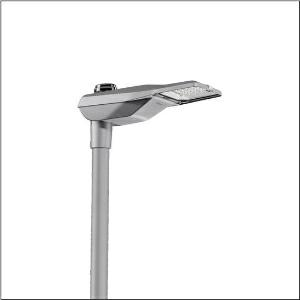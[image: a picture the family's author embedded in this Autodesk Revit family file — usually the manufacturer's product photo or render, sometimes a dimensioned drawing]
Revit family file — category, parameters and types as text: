
# Revit family: streetlight_sl_21_micro___stw1_0a_5xe5e37n08db_8c5c
name_source: partatom
category: Lighting Fixtures
units: mm (PartAtom-declared; Revit-internal decimal feet)

## family parameters
Cut with Voids When Loaded = No
Host = Face
Light Source = No
Part Type = Normal
Room Calculation Point = No
Round Connector Dimension = Use Diameter
Shared = No

## types (1)
- --- (1 x LED, 5110 lm, 39.1 W, 3000K)
    Apparent Load = 39 VA
    CIE Flux Codes = 38 75 98 100 100
    Color Rendering = 70
    Color Temperature = 3000K
    Default Elevation = 1800 mm
    Description = Streetlight SL 21 micro, mast luminaire, primary light control with lens, of PMMA, primary optical cover: cover, of toughened safety glass, transparent, light distribution: STW1.0a, light emission: direct distribution, primary light characteristic: asymmetric, installation type: post-top, LED, 3G 1.5mm², High Power LED, rated luminous flux: 5.110lm, luminous efficacy: 131lm/W, light colour: 730, colour temperature: 3000K, control: overheat protection, presetting dimming linear, constant luminous flux control, time-dependent luminous flux control, flexible luminous flux parameterisation, mains connection: 230..240V, AC, 50/60Hz, connection cable pre-assembled, cable length: 6,5m, wiring characteristics: H07RN-F, start of lifetime: 39W, end of service life: 41W, reduction: 18W, luminaire housing, of diecast aluminium (EN AC-44300), powder-coated, Siteco® metallic grey (DB 702S), corrosivity category C5 mid according to DIN EN ISO 12944, multi-level sealing system, sealing non-destructively replaceable, inclination adjustable: 0°, 5°, 10°, 15°, length: 528mm, width: 235mm, height: 110mm, spigot size: 76/60mm (post-top), protection rating (complete): IP66, insulation class (complete): insulation class I (protective earthing), certification: CE, ENEC, ENEC+, VDE, impact resistance: IK09, permissible operating ambient temperature for outdoor applications: -40..+50°C, standard-compliant lighting for roads and squares, packaging unit: 1 piece

Light Distribution: STW1.0a
    Height = 110 mm
    Lamp = 1 x LED
    Lamp Light Flux = 5110 lm
    Lamp Power = 39.1 W
    Lamp count = 1
    Length = 528 mm
    Luminous efficacy = 131 lm/W
    Manufacturer = Siteco
    ModVariant = No
    Model = 5XE5E37N08DB
    Number of Poles = 1
    OnlyDefault = Yes
    Power Factor = 1
    Product Name = Streetlight SL 21 micro | STW1.0a
    Product group = mast luminaire | pylon top
    ProductGroupID = 6100
    Protection Class = Protection class I
    Protection Degree = IP 66
    RLX_Detail_Level = 1
    RLX_Emergency_Light_Flux = 0 lm
    RLX_Emergency_Type = 0
    RLX_Emergency_Type_DB = No
    RlxData = <blob elided: 99193 chars, md5=ef52ab22>
    Socket = socket
    Standby Power = 0 W
    System Light Flux = 5110 lm
    System Power = 39 W
    Type Comments = factory setting: luminous flux: 100 % | dim-lin: 254 | 765 mA
    Type Image = l_1294375.jpg
    URL = http://relux.com
    VarID = @adj_067157
    Voltage = 0 V
    Weight = 0.00 kg
    Width = 235 mm

## geometry (parser evidence)
native form markers: Blend x4, Sweep x9
no freeform markers — native parametric forms only
